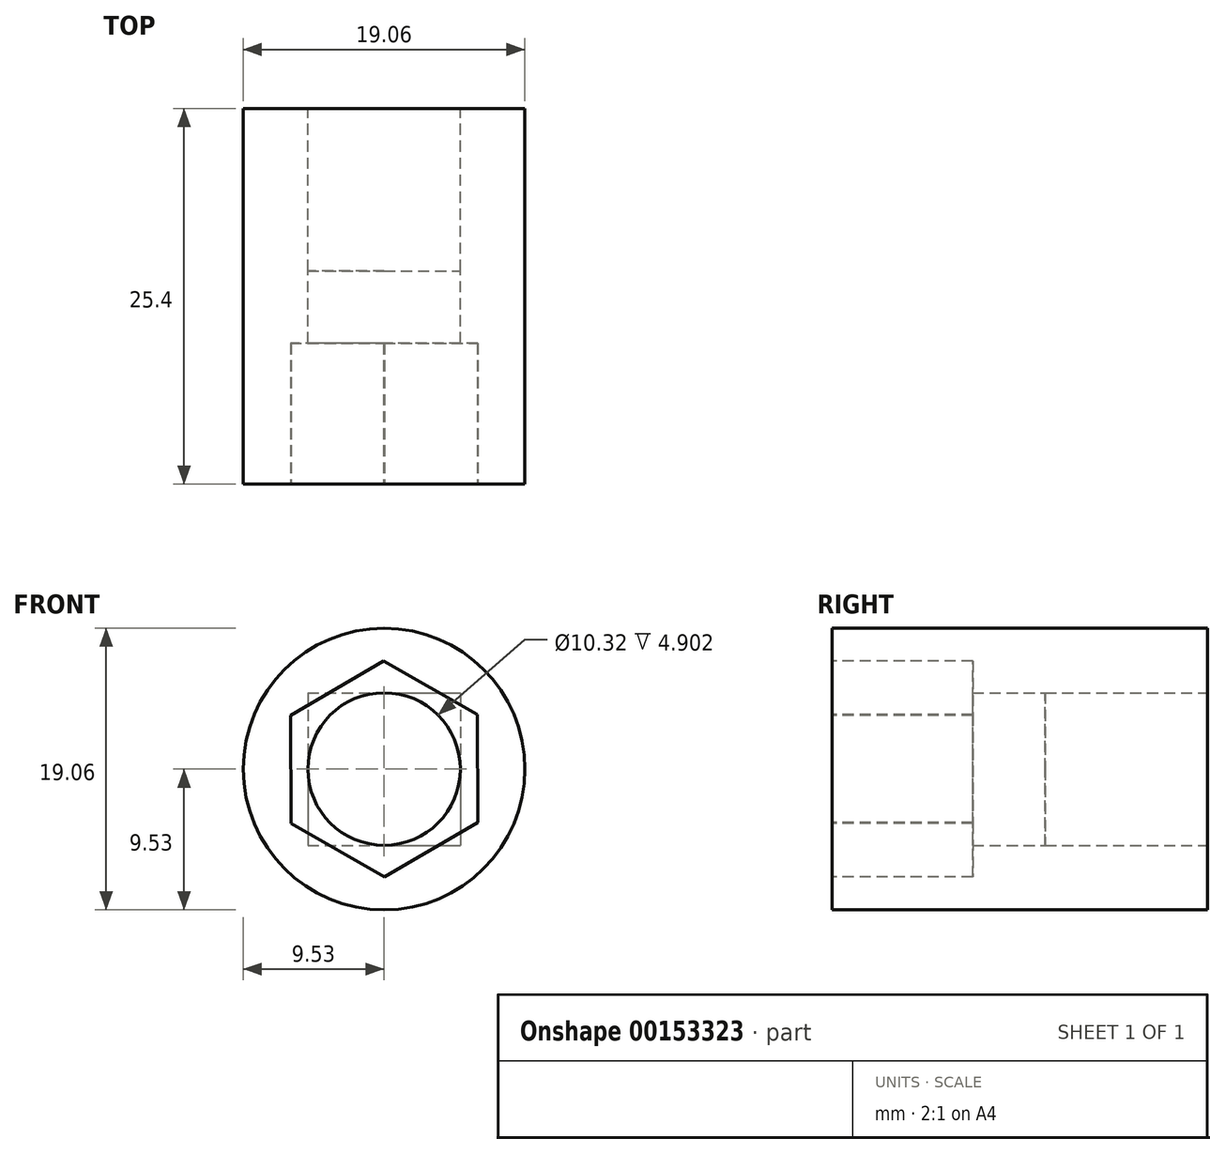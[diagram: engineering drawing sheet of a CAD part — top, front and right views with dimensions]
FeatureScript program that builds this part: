
annotation { "Feature Type Name" : "Feature", "Feature Type Description" : "" }
export const myFeature = defineFeature(function(context is Context, id is Id, definition is map)
    precondition{}
    {
        {
            var Q0;
            Q0=qCreatedBy(makeId("Front.planeOp"),FACE);
            var sketch = newSketch(context, id + "F0", { "sketchPlane" : qUnion([Q0])});
            skCircle(sketch, "E0", {"center": v(0, 0) * mm, "radius": 9.53 * mm});
            skSolve(sketch);
        }
        {
            var Q0;
            Q0 = qSketchRegion(id + "F0", true);
            extrude(context, id + "F1", {"entities" : qUnion([Q0]), "depth" : 25.4 * mm});
        }
        {
            var Q0;
            Q0=makeQuery(id+"F1.opExtrude","CAP_FACE",FACE,{"disambiguationData":[OSD([sQuery(id+"F0.wireOp",EDGE,"E0")])],"isStart":false});
            var sketch = newSketch(context, id + "F2", { "sketchPlane" : qUnion([Q0])});
            skCircle(sketch, "E1.cCircle", {"center": v(0, 0) * mm, "radius": 6.32 * mm, "construction": true});
            skLineSegment(sketch, "E1.0", {"start": v(-0.03, 7.3) * mm, "end": v(6.31, 3.67) * mm});
            skLineSegment(sketch, "E1.1", {"start": v(6.31, 3.67) * mm, "end": v(6.34, -3.63) * mm});
            skLineSegment(sketch, "E1.2", {"start": v(6.34, -3.63) * mm, "end": v(0.03, -7.3) * mm});
            skLineSegment(sketch, "E1.3", {"start": v(0.03, -7.3) * mm, "end": v(-6.31, -3.67) * mm});
            skLineSegment(sketch, "E1.4", {"start": v(-6.31, -3.67) * mm, "end": v(-6.34, 3.63) * mm});
            skLineSegment(sketch, "E1.5", {"start": v(-6.34, 3.63) * mm, "end": v(-0.03, 7.3) * mm});
            skPoint(sketch, "E1.0.midPoint", {"position": v(3.14, 5.49) * mm});
            skSolve(sketch);
        }
        {
            var Q0;
            Q0 = qSketchRegion(id + "F2", true);
            extrude(context, id + "F3", {"entities" : qUnion([Q0]), "operationType" : NewBodyOperationType.REMOVE, "oppositeDirection" : true, "depth" : 9.52 * mm});
        }
        {
            var Q0;
            Q0=makeQuery(id+"F1.opExtrude","CAP_FACE",FACE,{"disambiguationData":[OSD([sQuery(id+"F0.wireOp",EDGE,"E0")])],"isStart":true});
            var sketch = newSketch(context, id + "F4", { "sketchPlane" : qUnion([Q0])});
            skCircle(sketch, "E2", {"center": v(0, 0) * mm, "radius": 5.16 * mm});
            skSolve(sketch);
        }
        {
            var Q0;
            Q0=qCreatedBy(makeId("Front.planeOp"),FACE);
            var sketch = newSketch(context, id + "F5", { "sketchPlane" : qUnion([Q0])});
            skLineSegment(sketch, "E3.bottom", {"start": v(-5.16, 5.16) * mm, "end": v(5.16, 5.16) * mm});
            skLineSegment(sketch, "E3.top", {"start": v(-5.16, -5.16) * mm, "end": v(5.16, -5.16) * mm});
            skLineSegment(sketch, "E3.left", {"start": v(-5.16, 5.16) * mm, "end": v(-5.16, -5.16) * mm});
            skLineSegment(sketch, "E3.right", {"start": v(5.16, 5.16) * mm, "end": v(5.16, -5.16) * mm});
            skPoint(sketch, "E3.middle", {"position": v(0, 0) * mm});
            skSolve(sketch);
        }
        {
            var Q0;
            Q0 = qSketchRegion(id + "F5", true);
            extrude(context, id + "F6", {"entities" : qUnion([Q0]), "operationType" : NewBodyOperationType.REMOVE, "depth" : 10.97 * mm});
        }
        {
            var Q0;
            Q0 = qSketchRegion(id + "F4", true);
            extrude(context, id + "F7", {"entities" : qUnion([Q0]), "operationType" : NewBodyOperationType.REMOVE, "endBound" : BoundingType.THROUGH_ALL, "oppositeDirection" : true, "depth" : 25.4 * mm});
        }
    });
